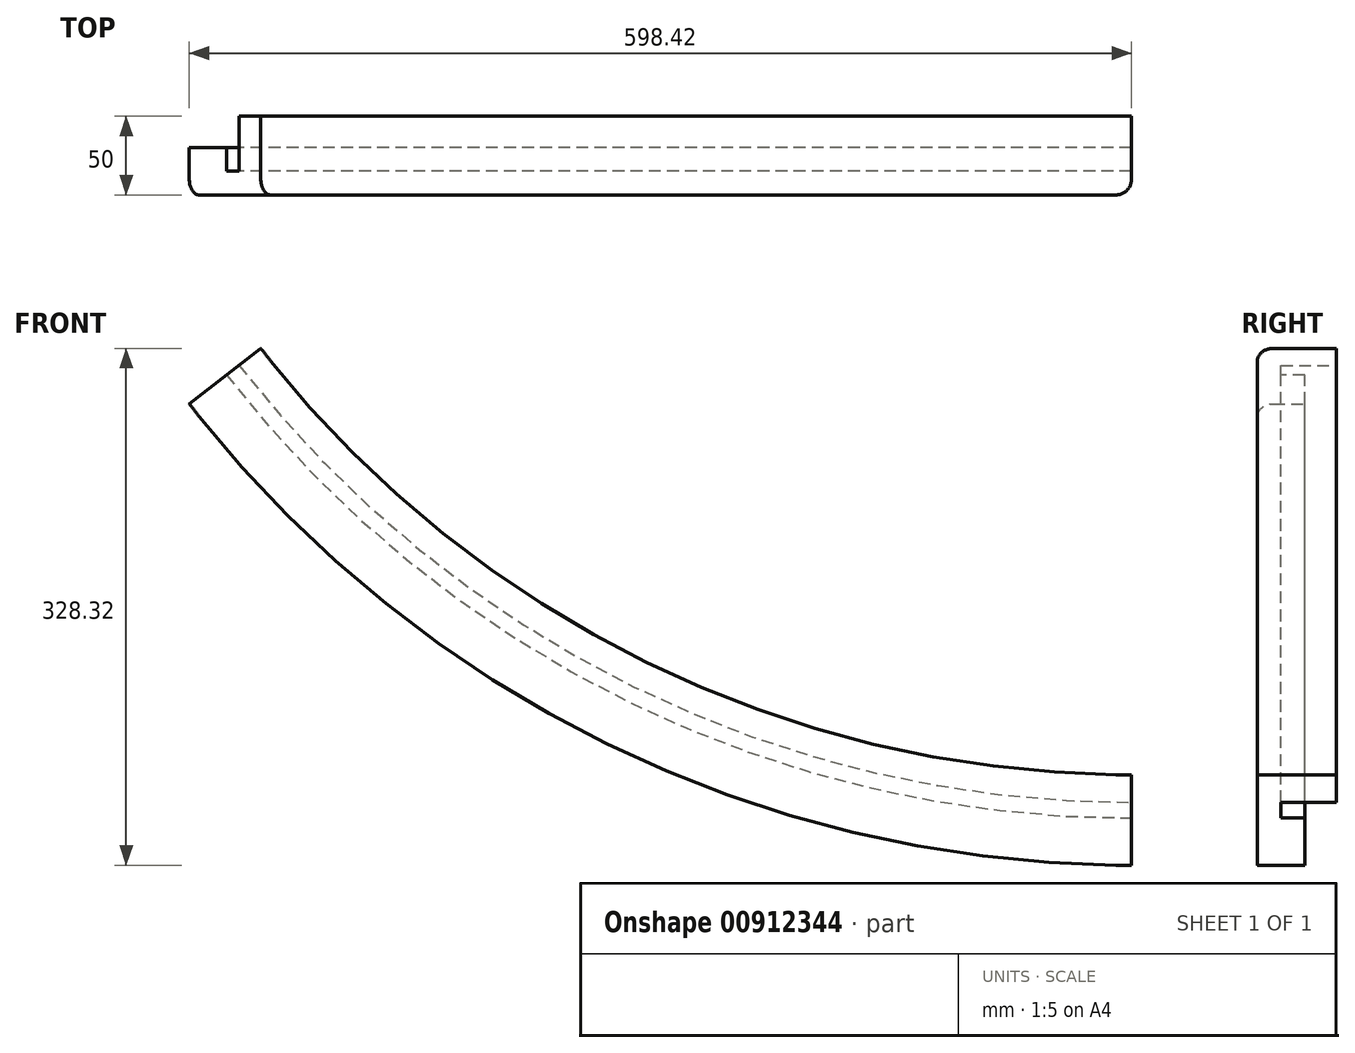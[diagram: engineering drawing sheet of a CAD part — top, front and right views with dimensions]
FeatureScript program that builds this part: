
annotation { "Feature Type Name" : "Feature", "Feature Type Description" : "" }
export const myFeature = defineFeature(function(context is Context, id is Id, definition is map)
    precondition{}
    {
        {
            var Q0;
            Q0=qCreatedBy(makeId("Front.planeOp"),FACE);
            var sketch = newSketch(context, id + "F0", { "sketchPlane" : qUnion([Q0])});
            skArc(sketch, "E0", {"start": v(-553, -429.18) * mm, "mid": v(-307.87, -628.66) * mm, "end": v(0, -700) * mm});
            skSolve(sketch);
        }
        {
            var Q0;
            Q0=qCreatedBy(makeId("Right.planeOp"),FACE);
            var sketch = newSketch(context, id + "F1", { "sketchPlane" : qUnion([Q0])});
            skLineSegment(sketch, "E1", {"start": v(0, -700) * mm, "end": v(-50, -700) * mm});
            skLineSegment(sketch, "E2", {"start": v(-50, -700) * mm, "end": v(-50, -757.5) * mm});
            skLineSegment(sketch, "E3", {"start": v(-50, -757.5) * mm, "end": v(-20, -757.5) * mm});
            skLineSegment(sketch, "E4", {"start": v(-20, -757.5) * mm, "end": v(-20, -727.5) * mm});
            skLineSegment(sketch, "E5", {"start": v(-20, -727.5) * mm, "end": v(-35, -727.5) * mm});
            skLineSegment(sketch, "E6", {"start": v(-35, -727.5) * mm, "end": v(-35, -717.5) * mm});
            skLineSegment(sketch, "E7", {"start": v(-35, -717.5) * mm, "end": v(0, -717.5) * mm});
            skLineSegment(sketch, "E8", {"start": v(0, -717.5) * mm, "end": v(0, -700) * mm});
            skSolve(sketch);
        }
        {
            var Q0;
            Q0=makeQuery(id+"F1.imprint","IMPRINT",FACE,{"disambiguationData":[TD([[makeQuery(id+"F1.imprint","IMPRINT",EDGE,{"derivedFrom":sQuery(id+"F1.wireOp",EDGE,"E1")}),1.0]])]});
            var Q1;
            Q1=sQuery(id+"F0.wireOp",EDGE,"E0");
            sweep(context, id + "F2", {"profiles" : qUnion([Q0]), "path" : qUnion([Q1])});
        }
        {
            var Q0;
            Q0=makeQuery(id+"F2.opSweep","CAP_EDGE",EDGE,{"disambiguationData":[OSD([sQuery(id+"F0.wireOp",VERTEX,"E0.start"),sQuery(id+"F1.wireOp",EDGE,"E2")])],"isStart":false});
            fillet(context, id + "F3", {"entities" : qUnion([Q0]), "radius" : 10 * mm, "tangentPropagation" : true, "allowEdgeOverflow" : false});
        }
        {
            var Q0;
            Q0=makeQuery(id+"F2.opSweep","CAP_EDGE",EDGE,{"disambiguationData":[OSD([sQuery(id+"F0.wireOp",VERTEX,"E0.end"),sQuery(id+"F1.wireOp",EDGE,"E2")])],"isStart":true});
            fillet(context, id + "F4", {"entities" : qUnion([Q0]), "radius" : 10 * mm, "tangentPropagation" : true, "allowEdgeOverflow" : false});
        }
    });
